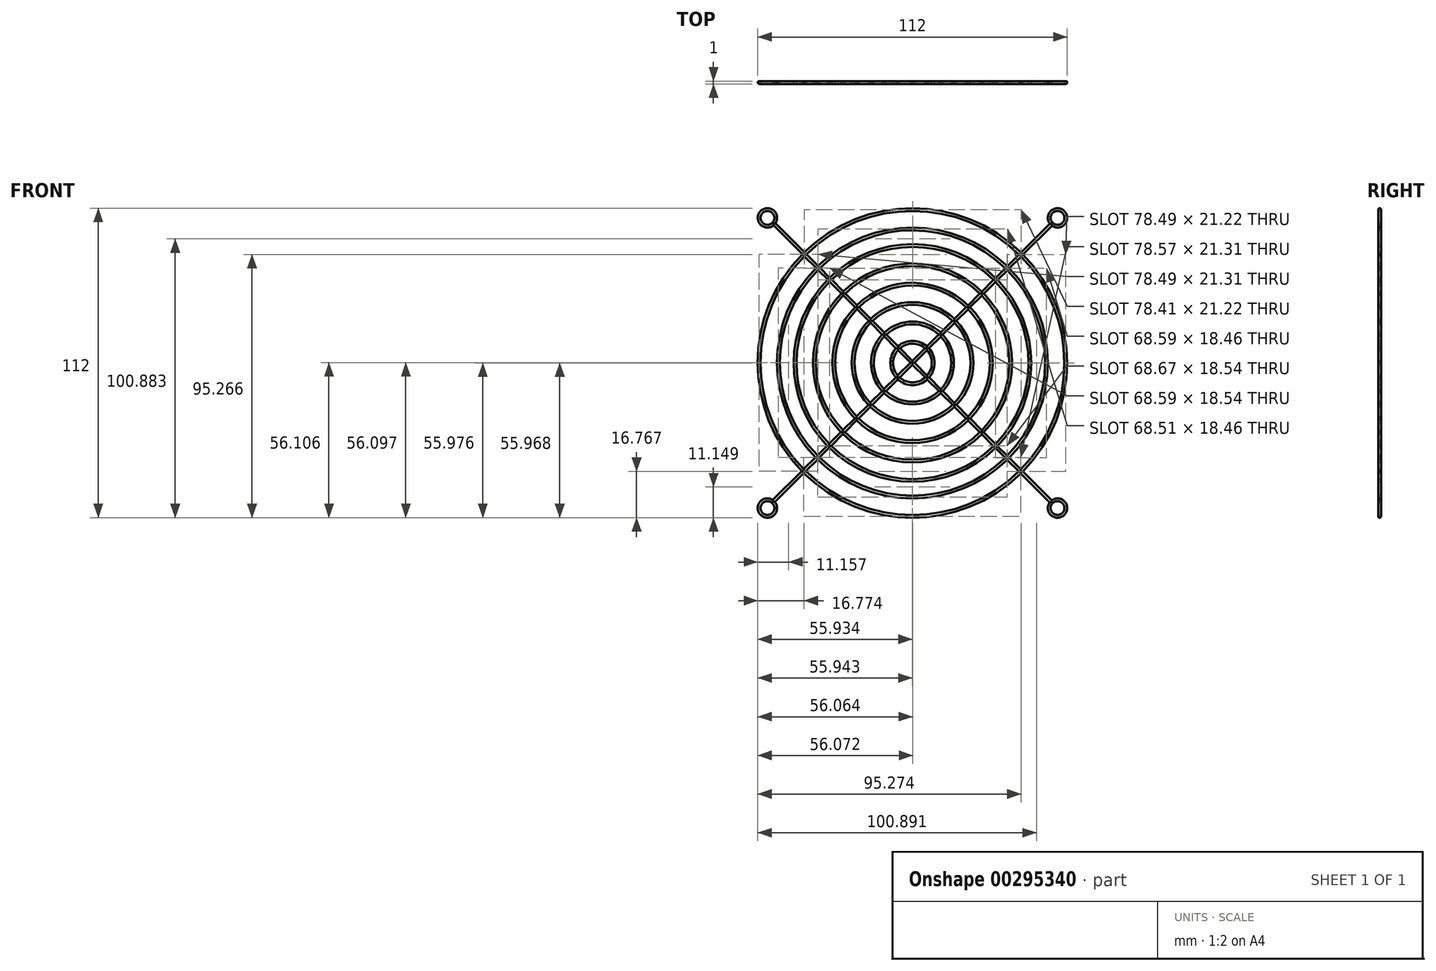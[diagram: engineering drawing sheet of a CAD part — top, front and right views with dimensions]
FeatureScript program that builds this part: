
annotation { "Feature Type Name" : "Feature", "Feature Type Description" : "" }
export const myFeature = defineFeature(function(context is Context, id is Id, definition is map)
    precondition{}
    {
        {
            var Q0;
            Q0=qCreatedBy(makeId("Front.planeOp"),FACE);
            var sketch = newSketch(context, id + "F0", { "sketchPlane" : qUnion([Q0])});
            skCircle(sketch, "E0", {"center": v(-12.88, 1.36) * mm, "radius": 7 * mm});
            skCircle(sketch, "E1", {"center": v(-12.88, 1.36) * mm, "radius": 8 * mm});
            skCircle(sketch, "E2", {"center": v(-12.88, 1.36) * mm, "radius": 14 * mm});
            skCircle(sketch, "E3", {"center": v(-12.88, 1.36) * mm, "radius": 15 * mm});
            skCircle(sketch, "E4", {"center": v(-12.88, 1.36) * mm, "radius": 21 * mm});
            skCircle(sketch, "E5", {"center": v(-12.88, 1.36) * mm, "radius": 22 * mm});
            skCircle(sketch, "E6", {"center": v(-12.88, 1.36) * mm, "radius": 28 * mm});
            skCircle(sketch, "E7", {"center": v(-12.88, 1.36) * mm, "radius": 29 * mm});
            skCircle(sketch, "E8", {"center": v(-12.88, 1.36) * mm, "radius": 35 * mm});
            skCircle(sketch, "E9", {"center": v(-12.88, 1.36) * mm, "radius": 36 * mm});
            skCircle(sketch, "E10", {"center": v(-12.88, 1.36) * mm, "radius": 42 * mm});
            skCircle(sketch, "E11", {"center": v(-12.88, 1.36) * mm, "radius": 43 * mm});
            skCircle(sketch, "E12", {"center": v(-12.88, 1.36) * mm, "radius": 48 * mm});
            skCircle(sketch, "E13", {"center": v(-12.88, 1.36) * mm, "radius": 49 * mm});
            skCircle(sketch, "E14", {"center": v(-12.88, 1.36) * mm, "radius": 55 * mm});
            skCircle(sketch, "E15", {"center": v(-12.88, 1.36) * mm, "radius": 56 * mm});
            skLineSegment(sketch, "E16.bottom", {"start": v(39.62, -51.14) * mm, "end": v(-65.38, -51.14) * mm, "construction": true});
            skLineSegment(sketch, "E16.top", {"start": v(39.62, 53.86) * mm, "end": v(-65.38, 53.86) * mm, "construction": true});
            skLineSegment(sketch, "E16.left", {"start": v(39.62, -51.14) * mm, "end": v(39.62, 53.86) * mm, "construction": true});
            skLineSegment(sketch, "E16.right", {"start": v(-65.38, -51.14) * mm, "end": v(-65.38, 53.86) * mm, "construction": true});
            skCircle(sketch, "E17", {"center": v(-65.38, 53.86) * mm, "radius": 2.5 * mm});
            skCircle(sketch, "E18", {"center": v(39.62, 53.86) * mm, "radius": 2.5 * mm});
            skCircle(sketch, "E19", {"center": v(39.62, -51.14) * mm, "radius": 2.5 * mm});
            skCircle(sketch, "E20", {"center": v(-65.38, -51.14) * mm, "radius": 2.5 * mm});
            skCircle(sketch, "E21", {"center": v(-65.38, 53.86) * mm, "radius": 3.5 * mm});
            skCircle(sketch, "E22", {"center": v(39.62, 53.86) * mm, "radius": 3.5 * mm});
            skCircle(sketch, "E23", {"center": v(39.62, -51.14) * mm, "radius": 3.5 * mm});
            skCircle(sketch, "E24", {"center": v(-65.38, -51.14) * mm, "radius": 3.5 * mm});
            skLineSegment(sketch, "E25", {"start": v(37.2, 51.33) * mm, "end": v(-63.03, -48.54) * mm, "construction": true});
            skLineSegment(sketch, "E26", {"start": v(-12.56, 1.04) * mm, "end": v(-62.69, -48.9) * mm});
            skLineSegment(sketch, "E27", {"start": v(-13.24, 1.78) * mm, "end": v(-63.43, -48.23) * mm});
            skLineSegment(sketch, "E28", {"start": v(-13.24, 1.78) * mm, "end": v(36.86, 51.7) * mm});
            skLineSegment(sketch, "E29", {"start": v(-12.56, 1.04) * mm, "end": v(37.58, 51.01) * mm});
            skLineSegment(sketch, "E30.1.0", {"start": v(-12.46, 1.72) * mm, "end": v(37.47, -48.38) * mm});
            skLineSegment(sketch, "E30.1.1", {"start": v(37.1, -48.72) * mm, "end": v(-62.78, 51.51) * mm, "construction": true});
            skLineSegment(sketch, "E30.1.2", {"start": v(-13.19, 1.04) * mm, "end": v(36.78, -49.1) * mm});
            skLineSegment(sketch, "E30.1.3", {"start": v(-13.19, 1.04) * mm, "end": v(-63.14, 51.17) * mm});
            skLineSegment(sketch, "E30.1.4", {"start": v(-12.46, 1.72) * mm, "end": v(-62.47, 51.91) * mm});
            skLineSegment(sketch, "E30.anchor1", {"start": v(-12.88, 1.36) * mm, "end": v(-12.56, 1.04) * mm, "construction": true});
            skLineSegment(sketch, "E30.anchor2", {"start": v(-12.88, 1.36) * mm, "end": v(-13.19, 1.04) * mm, "construction": true});
            skSolve(sketch);
        }
        {
            var Q0;
            {var subQ0=sQuery(id+"F0.wireOp",EDGE,"E28");var subQ1=sQuery(id+"F0.wireOp",EDGE,"E14");var subQ2=makeQuery(id+"F0.imprint","INTERSECT",VERTEX,{"derivedFrom":[subQ1,subQ0]});Q0=makeQuery(id+"F0.imprint","IMPRINT",FACE,{"disambiguationData":[TD([[makeQuery(id+"F0.imprint","IMPRINT",EDGE,{"disambiguationData":[TD([[subQ2,-1.0]])],"derivedFrom":subQ1}),-1.0]])]});}
            var Q1;
            {var subQ0=sQuery(id+"F0.wireOp",EDGE,"E29");var subQ1=sQuery(id+"F0.wireOp",EDGE,"E14");var subQ2=makeQuery(id+"F0.imprint","INTERSECT",VERTEX,{"derivedFrom":[subQ1,subQ0]});Q1=makeQuery(id+"F0.imprint","IMPRINT",FACE,{"disambiguationData":[TD([[makeQuery(id+"F0.imprint","IMPRINT",EDGE,{"disambiguationData":[TD([[subQ2,1.0]])],"derivedFrom":subQ1}),-1.0]])]});}
            var Q2;
            {var subQ0=sQuery(id+"F0.wireOp",EDGE,"E28");var subQ1=sQuery(id+"F0.wireOp",EDGE,"E15");var subQ2=makeQuery(id+"F0.imprint","INTERSECT",VERTEX,{"derivedFrom":[subQ1,subQ0]});Q2=makeQuery(id+"F0.imprint","IMPRINT",FACE,{"disambiguationData":[TD([[makeQuery(id+"F0.imprint","IMPRINT",EDGE,{"disambiguationData":[TD([[subQ2,1.0]])],"derivedFrom":subQ1}),-1.0]])]});}
            var Q3;
            {var subQ0=sQuery(id+"F0.wireOp",EDGE,"E28");var subQ1=sQuery(id+"F0.wireOp",EDGE,"E13");var subQ2=makeQuery(id+"F0.imprint","INTERSECT",VERTEX,{"derivedFrom":[subQ1,subQ0]});Q3=makeQuery(id+"F0.imprint","IMPRINT",FACE,{"disambiguationData":[TD([[makeQuery(id+"F0.imprint","IMPRINT",EDGE,{"disambiguationData":[TD([[subQ2,1.0]])],"derivedFrom":subQ1}),-1.0]])]});}
            var Q4;
            {var subQ0=sQuery(id+"F0.wireOp",EDGE,"E28");var subQ1=sQuery(id+"F0.wireOp",EDGE,"E14");var subQ2=makeQuery(id+"F0.imprint","INTERSECT",VERTEX,{"derivedFrom":[subQ1,subQ0]});Q4=makeQuery(id+"F0.imprint","IMPRINT",FACE,{"disambiguationData":[TD([[makeQuery(id+"F0.imprint","IMPRINT",EDGE,{"disambiguationData":[TD([[subQ2,1.0]])],"derivedFrom":subQ1}),-1.0]])]});}
            var Q5;
            {var subQ0=sQuery(id+"F0.wireOp",EDGE,"E28");var subQ1=sQuery(id+"F0.wireOp",EDGE,"E12");var subQ2=makeQuery(id+"F0.imprint","INTERSECT",VERTEX,{"derivedFrom":[subQ1,subQ0]});Q5=makeQuery(id+"F0.imprint","IMPRINT",FACE,{"disambiguationData":[TD([[makeQuery(id+"F0.imprint","IMPRINT",EDGE,{"disambiguationData":[TD([[subQ2,-1.0]])],"derivedFrom":subQ1}),-1.0]])]});}
            var Q6;
            {var subQ0=sQuery(id+"F0.wireOp",EDGE,"E29");var subQ1=sQuery(id+"F0.wireOp",EDGE,"E12");var subQ2=makeQuery(id+"F0.imprint","INTERSECT",VERTEX,{"derivedFrom":[subQ1,subQ0]});Q6=makeQuery(id+"F0.imprint","IMPRINT",FACE,{"disambiguationData":[TD([[makeQuery(id+"F0.imprint","IMPRINT",EDGE,{"disambiguationData":[TD([[subQ2,1.0]])],"derivedFrom":subQ1}),-1.0]])]});}
            var Q7;
            {var subQ0=sQuery(id+"F0.wireOp",EDGE,"E28");var subQ1=sQuery(id+"F0.wireOp",EDGE,"E12");var subQ2=makeQuery(id+"F0.imprint","INTERSECT",VERTEX,{"derivedFrom":[subQ1,subQ0]});Q7=makeQuery(id+"F0.imprint","IMPRINT",FACE,{"disambiguationData":[TD([[makeQuery(id+"F0.imprint","IMPRINT",EDGE,{"disambiguationData":[TD([[subQ2,1.0]])],"derivedFrom":subQ1}),-1.0]])]});}
            var Q8;
            {var subQ0=sQuery(id+"F0.wireOp",EDGE,"E28");var subQ1=sQuery(id+"F0.wireOp",EDGE,"E10");var subQ2=makeQuery(id+"F0.imprint","INTERSECT",VERTEX,{"derivedFrom":[subQ1,subQ0]});Q8=makeQuery(id+"F0.imprint","IMPRINT",FACE,{"disambiguationData":[TD([[makeQuery(id+"F0.imprint","IMPRINT",EDGE,{"disambiguationData":[TD([[subQ2,-1.0]])],"derivedFrom":subQ1}),-1.0]])]});}
            var Q9;
            {var subQ0=sQuery(id+"F0.wireOp",EDGE,"E29");var subQ1=sQuery(id+"F0.wireOp",EDGE,"E10");var subQ2=makeQuery(id+"F0.imprint","INTERSECT",VERTEX,{"derivedFrom":[subQ1,subQ0]});Q9=makeQuery(id+"F0.imprint","IMPRINT",FACE,{"disambiguationData":[TD([[makeQuery(id+"F0.imprint","IMPRINT",EDGE,{"disambiguationData":[TD([[subQ2,1.0]])],"derivedFrom":subQ1}),-1.0]])]});}
            var Q10;
            {var subQ0=sQuery(id+"F0.wireOp",EDGE,"E28");var subQ1=sQuery(id+"F0.wireOp",EDGE,"E10");var subQ2=makeQuery(id+"F0.imprint","INTERSECT",VERTEX,{"derivedFrom":[subQ1,subQ0]});Q10=makeQuery(id+"F0.imprint","IMPRINT",FACE,{"disambiguationData":[TD([[makeQuery(id+"F0.imprint","IMPRINT",EDGE,{"disambiguationData":[TD([[subQ2,1.0]])],"derivedFrom":subQ1}),-1.0]])]});}
            var Q11;
            {var subQ0=sQuery(id+"F0.wireOp",EDGE,"E28");var subQ1=sQuery(id+"F0.wireOp",EDGE,"E11");var subQ2=makeQuery(id+"F0.imprint","INTERSECT",VERTEX,{"derivedFrom":[subQ1,subQ0]});Q11=makeQuery(id+"F0.imprint","IMPRINT",FACE,{"disambiguationData":[TD([[makeQuery(id+"F0.imprint","IMPRINT",EDGE,{"disambiguationData":[TD([[subQ2,1.0]])],"derivedFrom":subQ1}),-1.0]])]});}
            var Q12;
            {var subQ0=sQuery(id+"F0.wireOp",EDGE,"E28");var subQ1=sQuery(id+"F0.wireOp",EDGE,"E9");var subQ2=makeQuery(id+"F0.imprint","INTERSECT",VERTEX,{"derivedFrom":[subQ1,subQ0]});Q12=makeQuery(id+"F0.imprint","IMPRINT",FACE,{"disambiguationData":[TD([[makeQuery(id+"F0.imprint","IMPRINT",EDGE,{"disambiguationData":[TD([[subQ2,1.0]])],"derivedFrom":subQ1}),-1.0]])]});}
            var Q13;
            {var subQ0=sQuery(id+"F0.wireOp",EDGE,"E29");var subQ1=sQuery(id+"F0.wireOp",EDGE,"E8");var subQ2=makeQuery(id+"F0.imprint","INTERSECT",VERTEX,{"derivedFrom":[subQ1,subQ0]});Q13=makeQuery(id+"F0.imprint","IMPRINT",FACE,{"disambiguationData":[TD([[makeQuery(id+"F0.imprint","IMPRINT",EDGE,{"disambiguationData":[TD([[subQ2,1.0]])],"derivedFrom":subQ1}),-1.0]])]});}
            var Q14;
            {var subQ0=sQuery(id+"F0.wireOp",EDGE,"E28");var subQ1=sQuery(id+"F0.wireOp",EDGE,"E7");var subQ2=makeQuery(id+"F0.imprint","INTERSECT",VERTEX,{"derivedFrom":[subQ1,subQ0]});Q14=makeQuery(id+"F0.imprint","IMPRINT",FACE,{"disambiguationData":[TD([[makeQuery(id+"F0.imprint","IMPRINT",EDGE,{"disambiguationData":[TD([[subQ2,1.0]])],"derivedFrom":subQ1}),-1.0]])]});}
            var Q15;
            {var subQ0=sQuery(id+"F0.wireOp",EDGE,"E28");var subQ1=sQuery(id+"F0.wireOp",EDGE,"E8");var subQ2=makeQuery(id+"F0.imprint","INTERSECT",VERTEX,{"derivedFrom":[subQ1,subQ0]});Q15=makeQuery(id+"F0.imprint","IMPRINT",FACE,{"disambiguationData":[TD([[makeQuery(id+"F0.imprint","IMPRINT",EDGE,{"disambiguationData":[TD([[subQ2,1.0]])],"derivedFrom":subQ1}),-1.0]])]});}
            var Q16;
            {var subQ0=sQuery(id+"F0.wireOp",EDGE,"E28");var subQ1=sQuery(id+"F0.wireOp",EDGE,"E8");var subQ2=makeQuery(id+"F0.imprint","INTERSECT",VERTEX,{"derivedFrom":[subQ1,subQ0]});Q16=makeQuery(id+"F0.imprint","IMPRINT",FACE,{"disambiguationData":[TD([[makeQuery(id+"F0.imprint","IMPRINT",EDGE,{"disambiguationData":[TD([[subQ2,-1.0]])],"derivedFrom":subQ1}),-1.0]])]});}
            var Q17;
            {var subQ0=sQuery(id+"F0.wireOp",EDGE,"E28");var subQ1=sQuery(id+"F0.wireOp",EDGE,"E6");var subQ2=makeQuery(id+"F0.imprint","INTERSECT",VERTEX,{"derivedFrom":[subQ1,subQ0]});Q17=makeQuery(id+"F0.imprint","IMPRINT",FACE,{"disambiguationData":[TD([[makeQuery(id+"F0.imprint","IMPRINT",EDGE,{"disambiguationData":[TD([[subQ2,-1.0]])],"derivedFrom":subQ1}),-1.0]])]});}
            var Q18;
            {var subQ0=sQuery(id+"F0.wireOp",EDGE,"E29");var subQ1=sQuery(id+"F0.wireOp",EDGE,"E6");var subQ2=makeQuery(id+"F0.imprint","INTERSECT",VERTEX,{"derivedFrom":[subQ1,subQ0]});Q18=makeQuery(id+"F0.imprint","IMPRINT",FACE,{"disambiguationData":[TD([[makeQuery(id+"F0.imprint","IMPRINT",EDGE,{"disambiguationData":[TD([[subQ2,1.0]])],"derivedFrom":subQ1}),-1.0]])]});}
            var Q19;
            {var subQ0=sQuery(id+"F0.wireOp",EDGE,"E28");var subQ1=sQuery(id+"F0.wireOp",EDGE,"E5");var subQ2=makeQuery(id+"F0.imprint","INTERSECT",VERTEX,{"derivedFrom":[subQ1,subQ0]});Q19=makeQuery(id+"F0.imprint","IMPRINT",FACE,{"disambiguationData":[TD([[makeQuery(id+"F0.imprint","IMPRINT",EDGE,{"disambiguationData":[TD([[subQ2,1.0]])],"derivedFrom":subQ1}),-1.0]])]});}
            var Q20;
            {var subQ0=sQuery(id+"F0.wireOp",EDGE,"E28");var subQ1=sQuery(id+"F0.wireOp",EDGE,"E6");var subQ2=makeQuery(id+"F0.imprint","INTERSECT",VERTEX,{"derivedFrom":[subQ1,subQ0]});Q20=makeQuery(id+"F0.imprint","IMPRINT",FACE,{"disambiguationData":[TD([[makeQuery(id+"F0.imprint","IMPRINT",EDGE,{"disambiguationData":[TD([[subQ2,1.0]])],"derivedFrom":subQ1}),-1.0]])]});}
            var Q21;
            {var subQ0=sQuery(id+"F0.wireOp",EDGE,"E28");var subQ1=sQuery(id+"F0.wireOp",EDGE,"E4");var subQ2=makeQuery(id+"F0.imprint","INTERSECT",VERTEX,{"derivedFrom":[subQ1,subQ0]});Q21=makeQuery(id+"F0.imprint","IMPRINT",FACE,{"disambiguationData":[TD([[makeQuery(id+"F0.imprint","IMPRINT",EDGE,{"disambiguationData":[TD([[subQ2,1.0]])],"derivedFrom":subQ1}),-1.0]])]});}
            var Q22;
            {var subQ0=sQuery(id+"F0.wireOp",EDGE,"E29");var subQ1=sQuery(id+"F0.wireOp",EDGE,"E4");var subQ2=makeQuery(id+"F0.imprint","INTERSECT",VERTEX,{"derivedFrom":[subQ1,subQ0]});Q22=makeQuery(id+"F0.imprint","IMPRINT",FACE,{"disambiguationData":[TD([[makeQuery(id+"F0.imprint","IMPRINT",EDGE,{"disambiguationData":[TD([[subQ2,1.0]])],"derivedFrom":subQ1}),-1.0]])]});}
            var Q23;
            {var subQ0=sQuery(id+"F0.wireOp",EDGE,"E28");var subQ1=sQuery(id+"F0.wireOp",EDGE,"E3");var subQ2=makeQuery(id+"F0.imprint","INTERSECT",VERTEX,{"derivedFrom":[subQ1,subQ0]});Q23=makeQuery(id+"F0.imprint","IMPRINT",FACE,{"disambiguationData":[TD([[makeQuery(id+"F0.imprint","IMPRINT",EDGE,{"disambiguationData":[TD([[subQ2,1.0]])],"derivedFrom":subQ1}),-1.0]])]});}
            var Q24;
            {var subQ0=sQuery(id+"F0.wireOp",EDGE,"E28");var subQ1=sQuery(id+"F0.wireOp",EDGE,"E4");var subQ2=makeQuery(id+"F0.imprint","INTERSECT",VERTEX,{"derivedFrom":[subQ1,subQ0]});Q24=makeQuery(id+"F0.imprint","IMPRINT",FACE,{"disambiguationData":[TD([[makeQuery(id+"F0.imprint","IMPRINT",EDGE,{"disambiguationData":[TD([[subQ2,-1.0]])],"derivedFrom":subQ1}),-1.0]])]});}
            var Q25;
            {var subQ0=sQuery(id+"F0.wireOp",EDGE,"E28");var subQ1=sQuery(id+"F0.wireOp",EDGE,"E2");var subQ2=makeQuery(id+"F0.imprint","INTERSECT",VERTEX,{"derivedFrom":[subQ1,subQ0]});Q25=makeQuery(id+"F0.imprint","IMPRINT",FACE,{"disambiguationData":[TD([[makeQuery(id+"F0.imprint","IMPRINT",EDGE,{"disambiguationData":[TD([[subQ2,1.0]])],"derivedFrom":subQ1}),-1.0]])]});}
            var Q26;
            {var subQ0=sQuery(id+"F0.wireOp",EDGE,"E29");var subQ1=sQuery(id+"F0.wireOp",EDGE,"E2");var subQ2=makeQuery(id+"F0.imprint","INTERSECT",VERTEX,{"derivedFrom":[subQ1,subQ0]});Q26=makeQuery(id+"F0.imprint","IMPRINT",FACE,{"disambiguationData":[TD([[makeQuery(id+"F0.imprint","IMPRINT",EDGE,{"disambiguationData":[TD([[subQ2,1.0]])],"derivedFrom":subQ1}),-1.0]])]});}
            var Q27;
            {var subQ0=sQuery(id+"F0.wireOp",EDGE,"E28");var subQ1=sQuery(id+"F0.wireOp",EDGE,"E2");var subQ2=makeQuery(id+"F0.imprint","INTERSECT",VERTEX,{"derivedFrom":[subQ1,subQ0]});Q27=makeQuery(id+"F0.imprint","IMPRINT",FACE,{"disambiguationData":[TD([[makeQuery(id+"F0.imprint","IMPRINT",EDGE,{"disambiguationData":[TD([[subQ2,-1.0]])],"derivedFrom":subQ1}),-1.0]])]});}
            var Q28;
            {var subQ0=sQuery(id+"F0.wireOp",EDGE,"E28");var subQ1=sQuery(id+"F0.wireOp",EDGE,"E1");var subQ2=makeQuery(id+"F0.imprint","INTERSECT",VERTEX,{"derivedFrom":[subQ1,subQ0]});Q28=makeQuery(id+"F0.imprint","IMPRINT",FACE,{"disambiguationData":[TD([[makeQuery(id+"F0.imprint","IMPRINT",EDGE,{"disambiguationData":[TD([[subQ2,1.0]])],"derivedFrom":subQ1}),-1.0]])]});}
            var Q29;
            {var subQ0=sQuery(id+"F0.wireOp",EDGE,"E28");var subQ1=sQuery(id+"F0.wireOp",EDGE,"E0");var subQ2=makeQuery(id+"F0.imprint","INTERSECT",VERTEX,{"derivedFrom":[subQ1,subQ0]});Q29=makeQuery(id+"F0.imprint","IMPRINT",FACE,{"disambiguationData":[TD([[makeQuery(id+"F0.imprint","IMPRINT",EDGE,{"disambiguationData":[TD([[subQ2,-1.0]])],"derivedFrom":subQ1}),-1.0]])]});}
            var Q30;
            {var subQ0=sQuery(id+"F0.wireOp",EDGE,"E29");var subQ1=sQuery(id+"F0.wireOp",EDGE,"E0");var subQ2=makeQuery(id+"F0.imprint","INTERSECT",VERTEX,{"derivedFrom":[subQ1,subQ0]});Q30=makeQuery(id+"F0.imprint","IMPRINT",FACE,{"disambiguationData":[TD([[makeQuery(id+"F0.imprint","IMPRINT",EDGE,{"disambiguationData":[TD([[subQ2,1.0]])],"derivedFrom":subQ1}),-1.0]])]});}
            var Q31;
            {var subQ0=sQuery(id+"F0.wireOp",EDGE,"E28");var subQ1=sQuery(id+"F0.wireOp",EDGE,"E0");var subQ2=makeQuery(id+"F0.imprint","INTERSECT",VERTEX,{"derivedFrom":[subQ1,subQ0]});Q31=makeQuery(id+"F0.imprint","IMPRINT",FACE,{"disambiguationData":[TD([[makeQuery(id+"F0.imprint","IMPRINT",EDGE,{"disambiguationData":[TD([[subQ2,1.0]])],"derivedFrom":subQ1}),-1.0]])]});}
            var Q32;
            {var subQ5=sQuery(id+"F0.wireOp",EDGE,"E28");var subQ6=sQuery(id+"F0.wireOp",EDGE,"E0");var subQ7=makeQuery(id+"F0.imprint","INTERSECT",VERTEX,{"derivedFrom":[subQ6,subQ5]});Q32=makeQuery(id+"F0.imprint","IMPRINT",FACE,{"disambiguationData":[TD([[makeQuery(id+"F0.imprint","IMPRINT",EDGE,{"disambiguationData":[TD([[subQ7,1.0]])],"derivedFrom":subQ6}),1.0]])]});}
            var Q33;
            {var subQ0=sQuery(id+"F0.wireOp",EDGE,"E29");var subQ1=sQuery(id+"F0.wireOp",EDGE,"E26");var subQ2=makeQuery(id+"F0.imprint","INTERSECT",VERTEX,{"derivedFrom":[subQ1,subQ0]});Q33=makeQuery(id+"F0.imprint","IMPRINT",FACE,{"disambiguationData":[TD([[makeQuery(id+"F0.imprint","IMPRINT",EDGE,{"disambiguationData":[TD([[subQ2,-1.0]])],"derivedFrom":subQ1}),-1.0]])]});}
            var Q34;
            {var subQ1=sQuery(id+"F0.wireOp",EDGE,"E0");var subQ7=sQuery(id+"F0.wireOp",EDGE,"E30.1.4");var subQ9=makeQuery(id+"F0.imprint","INTERSECT",VERTEX,{"derivedFrom":[subQ1,subQ7]});Q34=makeQuery(id+"F0.imprint","IMPRINT",FACE,{"disambiguationData":[TD([[makeQuery(id+"F0.imprint","IMPRINT",EDGE,{"disambiguationData":[TD([[subQ9,-1.0]])],"derivedFrom":subQ1}),1.0]])]});}
            var Q35;
            {var subQ1=sQuery(id+"F0.wireOp",EDGE,"E0");var subQ7=sQuery(id+"F0.wireOp",EDGE,"E30.1.2");var subQ9=makeQuery(id+"F0.imprint","INTERSECT",VERTEX,{"derivedFrom":[subQ1,subQ7]});Q35=makeQuery(id+"F0.imprint","IMPRINT",FACE,{"disambiguationData":[TD([[makeQuery(id+"F0.imprint","IMPRINT",EDGE,{"disambiguationData":[TD([[subQ9,-1.0]])],"derivedFrom":subQ1}),1.0]])]});}
            var Q36;
            {var subQ5=sQuery(id+"F0.wireOp",EDGE,"E0");var subQ7=sQuery(id+"F0.wireOp",EDGE,"E27");var subQ8=makeQuery(id+"F0.imprint","INTERSECT",VERTEX,{"derivedFrom":[subQ5,subQ7]});Q36=makeQuery(id+"F0.imprint","IMPRINT",FACE,{"disambiguationData":[TD([[makeQuery(id+"F0.imprint","IMPRINT",EDGE,{"disambiguationData":[TD([[subQ8,-1.0]])],"derivedFrom":subQ5}),1.0]])]});}
            var Q37;
            {var subQ0=sQuery(id+"F0.wireOp",EDGE,"E30.1.4");var subQ1=sQuery(id+"F0.wireOp",EDGE,"E0");var subQ2=makeQuery(id+"F0.imprint","INTERSECT",VERTEX,{"derivedFrom":[subQ1,subQ0]});Q37=makeQuery(id+"F0.imprint","IMPRINT",FACE,{"disambiguationData":[TD([[makeQuery(id+"F0.imprint","IMPRINT",EDGE,{"disambiguationData":[TD([[subQ2,-1.0]])],"derivedFrom":subQ1}),-1.0]])]});}
            var Q38;
            {var subQ0=sQuery(id+"F0.wireOp",EDGE,"E30.1.3");var subQ1=sQuery(id+"F0.wireOp",EDGE,"E0");var subQ2=makeQuery(id+"F0.imprint","INTERSECT",VERTEX,{"derivedFrom":[subQ1,subQ0]});Q38=makeQuery(id+"F0.imprint","IMPRINT",FACE,{"disambiguationData":[TD([[makeQuery(id+"F0.imprint","IMPRINT",EDGE,{"disambiguationData":[TD([[subQ2,-1.0]])],"derivedFrom":subQ1}),-1.0]])]});}
            var Q39;
            {var subQ0=sQuery(id+"F0.wireOp",EDGE,"E30.1.4");var subQ1=sQuery(id+"F0.wireOp",EDGE,"E1");var subQ2=makeQuery(id+"F0.imprint","INTERSECT",VERTEX,{"derivedFrom":[subQ1,subQ0]});Q39=makeQuery(id+"F0.imprint","IMPRINT",FACE,{"disambiguationData":[TD([[makeQuery(id+"F0.imprint","IMPRINT",EDGE,{"disambiguationData":[TD([[subQ2,-1.0]])],"derivedFrom":subQ1}),-1.0]])]});}
            var Q40;
            {var subQ0=sQuery(id+"F0.wireOp",EDGE,"E30.1.3");var subQ1=sQuery(id+"F0.wireOp",EDGE,"E2");var subQ2=makeQuery(id+"F0.imprint","INTERSECT",VERTEX,{"derivedFrom":[subQ1,subQ0]});Q40=makeQuery(id+"F0.imprint","IMPRINT",FACE,{"disambiguationData":[TD([[makeQuery(id+"F0.imprint","IMPRINT",EDGE,{"disambiguationData":[TD([[subQ2,-1.0]])],"derivedFrom":subQ1}),-1.0]])]});}
            var Q41;
            {var subQ0=sQuery(id+"F0.wireOp",EDGE,"E30.1.4");var subQ1=sQuery(id+"F0.wireOp",EDGE,"E2");var subQ2=makeQuery(id+"F0.imprint","INTERSECT",VERTEX,{"derivedFrom":[subQ1,subQ0]});Q41=makeQuery(id+"F0.imprint","IMPRINT",FACE,{"disambiguationData":[TD([[makeQuery(id+"F0.imprint","IMPRINT",EDGE,{"disambiguationData":[TD([[subQ2,-1.0]])],"derivedFrom":subQ1}),-1.0]])]});}
            var Q42;
            {var subQ0=sQuery(id+"F0.wireOp",EDGE,"E30.1.4");var subQ1=sQuery(id+"F0.wireOp",EDGE,"E3");var subQ2=makeQuery(id+"F0.imprint","INTERSECT",VERTEX,{"derivedFrom":[subQ1,subQ0]});Q42=makeQuery(id+"F0.imprint","IMPRINT",FACE,{"disambiguationData":[TD([[makeQuery(id+"F0.imprint","IMPRINT",EDGE,{"disambiguationData":[TD([[subQ2,-1.0]])],"derivedFrom":subQ1}),-1.0]])]});}
            var Q43;
            {var subQ0=sQuery(id+"F0.wireOp",EDGE,"E30.1.4");var subQ1=sQuery(id+"F0.wireOp",EDGE,"E4");var subQ2=makeQuery(id+"F0.imprint","INTERSECT",VERTEX,{"derivedFrom":[subQ1,subQ0]});Q43=makeQuery(id+"F0.imprint","IMPRINT",FACE,{"disambiguationData":[TD([[makeQuery(id+"F0.imprint","IMPRINT",EDGE,{"disambiguationData":[TD([[subQ2,-1.0]])],"derivedFrom":subQ1}),-1.0]])]});}
            var Q44;
            {var subQ0=sQuery(id+"F0.wireOp",EDGE,"E30.1.3");var subQ1=sQuery(id+"F0.wireOp",EDGE,"E4");var subQ2=makeQuery(id+"F0.imprint","INTERSECT",VERTEX,{"derivedFrom":[subQ1,subQ0]});Q44=makeQuery(id+"F0.imprint","IMPRINT",FACE,{"disambiguationData":[TD([[makeQuery(id+"F0.imprint","IMPRINT",EDGE,{"disambiguationData":[TD([[subQ2,-1.0]])],"derivedFrom":subQ1}),-1.0]])]});}
            var Q45;
            {var subQ0=sQuery(id+"F0.wireOp",EDGE,"E30.1.4");var subQ1=sQuery(id+"F0.wireOp",EDGE,"E5");var subQ2=makeQuery(id+"F0.imprint","INTERSECT",VERTEX,{"derivedFrom":[subQ1,subQ0]});Q45=makeQuery(id+"F0.imprint","IMPRINT",FACE,{"disambiguationData":[TD([[makeQuery(id+"F0.imprint","IMPRINT",EDGE,{"disambiguationData":[TD([[subQ2,-1.0]])],"derivedFrom":subQ1}),-1.0]])]});}
            var Q46;
            {var subQ0=sQuery(id+"F0.wireOp",EDGE,"E30.1.3");var subQ1=sQuery(id+"F0.wireOp",EDGE,"E6");var subQ2=makeQuery(id+"F0.imprint","INTERSECT",VERTEX,{"derivedFrom":[subQ1,subQ0]});Q46=makeQuery(id+"F0.imprint","IMPRINT",FACE,{"disambiguationData":[TD([[makeQuery(id+"F0.imprint","IMPRINT",EDGE,{"disambiguationData":[TD([[subQ2,-1.0]])],"derivedFrom":subQ1}),-1.0]])]});}
            var Q47;
            {var subQ0=sQuery(id+"F0.wireOp",EDGE,"E30.1.4");var subQ1=sQuery(id+"F0.wireOp",EDGE,"E6");var subQ2=makeQuery(id+"F0.imprint","INTERSECT",VERTEX,{"derivedFrom":[subQ1,subQ0]});Q47=makeQuery(id+"F0.imprint","IMPRINT",FACE,{"disambiguationData":[TD([[makeQuery(id+"F0.imprint","IMPRINT",EDGE,{"disambiguationData":[TD([[subQ2,-1.0]])],"derivedFrom":subQ1}),-1.0]])]});}
            var Q48;
            {var subQ0=sQuery(id+"F0.wireOp",EDGE,"E30.1.4");var subQ1=sQuery(id+"F0.wireOp",EDGE,"E7");var subQ2=makeQuery(id+"F0.imprint","INTERSECT",VERTEX,{"derivedFrom":[subQ1,subQ0]});Q48=makeQuery(id+"F0.imprint","IMPRINT",FACE,{"disambiguationData":[TD([[makeQuery(id+"F0.imprint","IMPRINT",EDGE,{"disambiguationData":[TD([[subQ2,-1.0]])],"derivedFrom":subQ1}),-1.0]])]});}
            var Q49;
            {var subQ0=sQuery(id+"F0.wireOp",EDGE,"E30.1.4");var subQ1=sQuery(id+"F0.wireOp",EDGE,"E8");var subQ2=makeQuery(id+"F0.imprint","INTERSECT",VERTEX,{"derivedFrom":[subQ1,subQ0]});Q49=makeQuery(id+"F0.imprint","IMPRINT",FACE,{"disambiguationData":[TD([[makeQuery(id+"F0.imprint","IMPRINT",EDGE,{"disambiguationData":[TD([[subQ2,-1.0]])],"derivedFrom":subQ1}),-1.0]])]});}
            var Q50;
            {var subQ0=sQuery(id+"F0.wireOp",EDGE,"E30.1.3");var subQ1=sQuery(id+"F0.wireOp",EDGE,"E8");var subQ2=makeQuery(id+"F0.imprint","INTERSECT",VERTEX,{"derivedFrom":[subQ1,subQ0]});Q50=makeQuery(id+"F0.imprint","IMPRINT",FACE,{"disambiguationData":[TD([[makeQuery(id+"F0.imprint","IMPRINT",EDGE,{"disambiguationData":[TD([[subQ2,-1.0]])],"derivedFrom":subQ1}),-1.0]])]});}
            var Q51;
            {var subQ0=sQuery(id+"F0.wireOp",EDGE,"E30.1.4");var subQ1=sQuery(id+"F0.wireOp",EDGE,"E9");var subQ2=makeQuery(id+"F0.imprint","INTERSECT",VERTEX,{"derivedFrom":[subQ1,subQ0]});Q51=makeQuery(id+"F0.imprint","IMPRINT",FACE,{"disambiguationData":[TD([[makeQuery(id+"F0.imprint","IMPRINT",EDGE,{"disambiguationData":[TD([[subQ2,-1.0]])],"derivedFrom":subQ1}),-1.0]])]});}
            var Q52;
            {var subQ0=sQuery(id+"F0.wireOp",EDGE,"E30.1.4");var subQ1=sQuery(id+"F0.wireOp",EDGE,"E10");var subQ2=makeQuery(id+"F0.imprint","INTERSECT",VERTEX,{"derivedFrom":[subQ1,subQ0]});Q52=makeQuery(id+"F0.imprint","IMPRINT",FACE,{"disambiguationData":[TD([[makeQuery(id+"F0.imprint","IMPRINT",EDGE,{"disambiguationData":[TD([[subQ2,-1.0]])],"derivedFrom":subQ1}),-1.0]])]});}
            var Q53;
            {var subQ0=sQuery(id+"F0.wireOp",EDGE,"E30.1.3");var subQ1=sQuery(id+"F0.wireOp",EDGE,"E10");var subQ2=makeQuery(id+"F0.imprint","INTERSECT",VERTEX,{"derivedFrom":[subQ1,subQ0]});Q53=makeQuery(id+"F0.imprint","IMPRINT",FACE,{"disambiguationData":[TD([[makeQuery(id+"F0.imprint","IMPRINT",EDGE,{"disambiguationData":[TD([[subQ2,-1.0]])],"derivedFrom":subQ1}),-1.0]])]});}
            var Q54;
            {var subQ0=sQuery(id+"F0.wireOp",EDGE,"E30.1.4");var subQ1=sQuery(id+"F0.wireOp",EDGE,"E11");var subQ2=makeQuery(id+"F0.imprint","INTERSECT",VERTEX,{"derivedFrom":[subQ1,subQ0]});Q54=makeQuery(id+"F0.imprint","IMPRINT",FACE,{"disambiguationData":[TD([[makeQuery(id+"F0.imprint","IMPRINT",EDGE,{"disambiguationData":[TD([[subQ2,-1.0]])],"derivedFrom":subQ1}),-1.0]])]});}
            var Q55;
            {var subQ0=sQuery(id+"F0.wireOp",EDGE,"E30.1.4");var subQ1=sQuery(id+"F0.wireOp",EDGE,"E12");var subQ2=makeQuery(id+"F0.imprint","INTERSECT",VERTEX,{"derivedFrom":[subQ1,subQ0]});Q55=makeQuery(id+"F0.imprint","IMPRINT",FACE,{"disambiguationData":[TD([[makeQuery(id+"F0.imprint","IMPRINT",EDGE,{"disambiguationData":[TD([[subQ2,-1.0]])],"derivedFrom":subQ1}),-1.0]])]});}
            var Q56;
            {var subQ0=sQuery(id+"F0.wireOp",EDGE,"E30.1.3");var subQ1=sQuery(id+"F0.wireOp",EDGE,"E12");var subQ2=makeQuery(id+"F0.imprint","INTERSECT",VERTEX,{"derivedFrom":[subQ1,subQ0]});Q56=makeQuery(id+"F0.imprint","IMPRINT",FACE,{"disambiguationData":[TD([[makeQuery(id+"F0.imprint","IMPRINT",EDGE,{"disambiguationData":[TD([[subQ2,-1.0]])],"derivedFrom":subQ1}),-1.0]])]});}
            var Q57;
            {var subQ0=sQuery(id+"F0.wireOp",EDGE,"E30.1.4");var subQ1=sQuery(id+"F0.wireOp",EDGE,"E13");var subQ2=makeQuery(id+"F0.imprint","INTERSECT",VERTEX,{"derivedFrom":[subQ1,subQ0]});Q57=makeQuery(id+"F0.imprint","IMPRINT",FACE,{"disambiguationData":[TD([[makeQuery(id+"F0.imprint","IMPRINT",EDGE,{"disambiguationData":[TD([[subQ2,-1.0]])],"derivedFrom":subQ1}),-1.0]])]});}
            var Q58;
            {var subQ0=sQuery(id+"F0.wireOp",EDGE,"E30.1.4");var subQ1=sQuery(id+"F0.wireOp",EDGE,"E14");var subQ2=makeQuery(id+"F0.imprint","INTERSECT",VERTEX,{"derivedFrom":[subQ1,subQ0]});Q58=makeQuery(id+"F0.imprint","IMPRINT",FACE,{"disambiguationData":[TD([[makeQuery(id+"F0.imprint","IMPRINT",EDGE,{"disambiguationData":[TD([[subQ2,-1.0]])],"derivedFrom":subQ1}),-1.0]])]});}
            var Q59;
            {var subQ0=sQuery(id+"F0.wireOp",EDGE,"E30.1.3");var subQ1=sQuery(id+"F0.wireOp",EDGE,"E14");var subQ2=makeQuery(id+"F0.imprint","INTERSECT",VERTEX,{"derivedFrom":[subQ1,subQ0]});Q59=makeQuery(id+"F0.imprint","IMPRINT",FACE,{"disambiguationData":[TD([[makeQuery(id+"F0.imprint","IMPRINT",EDGE,{"disambiguationData":[TD([[subQ2,-1.0]])],"derivedFrom":subQ1}),-1.0]])]});}
            var Q60;
            {var subQ0=sQuery(id+"F0.wireOp",EDGE,"E30.1.4");var subQ1=sQuery(id+"F0.wireOp",EDGE,"E15");var subQ2=makeQuery(id+"F0.imprint","INTERSECT",VERTEX,{"derivedFrom":[subQ1,subQ0]});Q60=makeQuery(id+"F0.imprint","IMPRINT",FACE,{"disambiguationData":[TD([[makeQuery(id+"F0.imprint","IMPRINT",EDGE,{"disambiguationData":[TD([[subQ2,-1.0]])],"derivedFrom":subQ1}),-1.0]])]});}
            var Q61;
            Q61=makeQuery(id+"F0.imprint","IMPRINT",FACE,{"disambiguationData":[TD([[makeQuery(id+"F0.imprint","IMPRINT",EDGE,{"derivedFrom":sQuery(id+"F0.wireOp",EDGE,"E17")}),-1.0]])]});
            var Q62;
            Q62=makeQuery(id+"F0.imprint","IMPRINT",FACE,{"disambiguationData":[TD([[makeQuery(id+"F0.imprint","IMPRINT",EDGE,{"derivedFrom":sQuery(id+"F0.wireOp",EDGE,"E18")}),-1.0]])]});
            var Q63;
            {var subQ0=sQuery(id+"F0.wireOp",EDGE,"E26");var subQ1=sQuery(id+"F0.wireOp",EDGE,"E0");var subQ2=makeQuery(id+"F0.imprint","INTERSECT",VERTEX,{"derivedFrom":[subQ1,subQ0]});Q63=makeQuery(id+"F0.imprint","IMPRINT",FACE,{"disambiguationData":[TD([[makeQuery(id+"F0.imprint","IMPRINT",EDGE,{"disambiguationData":[TD([[subQ2,-1.0]])],"derivedFrom":subQ1}),-1.0]])]});}
            var Q64;
            {var subQ0=sQuery(id+"F0.wireOp",EDGE,"E30.1.2");var subQ1=sQuery(id+"F0.wireOp",EDGE,"E0");var subQ2=makeQuery(id+"F0.imprint","INTERSECT",VERTEX,{"derivedFrom":[subQ1,subQ0]});Q64=makeQuery(id+"F0.imprint","IMPRINT",FACE,{"disambiguationData":[TD([[makeQuery(id+"F0.imprint","IMPRINT",EDGE,{"disambiguationData":[TD([[subQ2,-1.0]])],"derivedFrom":subQ1}),-1.0]])]});}
            var Q65;
            {var subQ0=sQuery(id+"F0.wireOp",EDGE,"E30.1.2");var subQ1=sQuery(id+"F0.wireOp",EDGE,"E1");var subQ2=makeQuery(id+"F0.imprint","INTERSECT",VERTEX,{"derivedFrom":[subQ1,subQ0]});Q65=makeQuery(id+"F0.imprint","IMPRINT",FACE,{"disambiguationData":[TD([[makeQuery(id+"F0.imprint","IMPRINT",EDGE,{"disambiguationData":[TD([[subQ2,-1.0]])],"derivedFrom":subQ1}),-1.0]])]});}
            var Q66;
            {var subQ0=sQuery(id+"F0.wireOp",EDGE,"E26");var subQ1=sQuery(id+"F0.wireOp",EDGE,"E2");var subQ2=makeQuery(id+"F0.imprint","INTERSECT",VERTEX,{"derivedFrom":[subQ1,subQ0]});Q66=makeQuery(id+"F0.imprint","IMPRINT",FACE,{"disambiguationData":[TD([[makeQuery(id+"F0.imprint","IMPRINT",EDGE,{"disambiguationData":[TD([[subQ2,-1.0]])],"derivedFrom":subQ1}),-1.0]])]});}
            var Q67;
            {var subQ0=sQuery(id+"F0.wireOp",EDGE,"E30.1.2");var subQ1=sQuery(id+"F0.wireOp",EDGE,"E2");var subQ2=makeQuery(id+"F0.imprint","INTERSECT",VERTEX,{"derivedFrom":[subQ1,subQ0]});Q67=makeQuery(id+"F0.imprint","IMPRINT",FACE,{"disambiguationData":[TD([[makeQuery(id+"F0.imprint","IMPRINT",EDGE,{"disambiguationData":[TD([[subQ2,-1.0]])],"derivedFrom":subQ1}),-1.0]])]});}
            var Q68;
            {var subQ0=sQuery(id+"F0.wireOp",EDGE,"E30.1.2");var subQ1=sQuery(id+"F0.wireOp",EDGE,"E3");var subQ2=makeQuery(id+"F0.imprint","INTERSECT",VERTEX,{"derivedFrom":[subQ1,subQ0]});Q68=makeQuery(id+"F0.imprint","IMPRINT",FACE,{"disambiguationData":[TD([[makeQuery(id+"F0.imprint","IMPRINT",EDGE,{"disambiguationData":[TD([[subQ2,-1.0]])],"derivedFrom":subQ1}),-1.0]])]});}
            var Q69;
            {var subQ0=sQuery(id+"F0.wireOp",EDGE,"E30.1.2");var subQ1=sQuery(id+"F0.wireOp",EDGE,"E4");var subQ2=makeQuery(id+"F0.imprint","INTERSECT",VERTEX,{"derivedFrom":[subQ1,subQ0]});Q69=makeQuery(id+"F0.imprint","IMPRINT",FACE,{"disambiguationData":[TD([[makeQuery(id+"F0.imprint","IMPRINT",EDGE,{"disambiguationData":[TD([[subQ2,-1.0]])],"derivedFrom":subQ1}),-1.0]])]});}
            var Q70;
            {var subQ0=sQuery(id+"F0.wireOp",EDGE,"E30.1.2");var subQ1=sQuery(id+"F0.wireOp",EDGE,"E5");var subQ2=makeQuery(id+"F0.imprint","INTERSECT",VERTEX,{"derivedFrom":[subQ1,subQ0]});Q70=makeQuery(id+"F0.imprint","IMPRINT",FACE,{"disambiguationData":[TD([[makeQuery(id+"F0.imprint","IMPRINT",EDGE,{"disambiguationData":[TD([[subQ2,-1.0]])],"derivedFrom":subQ1}),-1.0]])]});}
            var Q71;
            {var subQ0=sQuery(id+"F0.wireOp",EDGE,"E26");var subQ1=sQuery(id+"F0.wireOp",EDGE,"E4");var subQ2=makeQuery(id+"F0.imprint","INTERSECT",VERTEX,{"derivedFrom":[subQ1,subQ0]});Q71=makeQuery(id+"F0.imprint","IMPRINT",FACE,{"disambiguationData":[TD([[makeQuery(id+"F0.imprint","IMPRINT",EDGE,{"disambiguationData":[TD([[subQ2,-1.0]])],"derivedFrom":subQ1}),-1.0]])]});}
            var Q72;
            {var subQ0=sQuery(id+"F0.wireOp",EDGE,"E30.1.2");var subQ1=sQuery(id+"F0.wireOp",EDGE,"E6");var subQ2=makeQuery(id+"F0.imprint","INTERSECT",VERTEX,{"derivedFrom":[subQ1,subQ0]});Q72=makeQuery(id+"F0.imprint","IMPRINT",FACE,{"disambiguationData":[TD([[makeQuery(id+"F0.imprint","IMPRINT",EDGE,{"disambiguationData":[TD([[subQ2,-1.0]])],"derivedFrom":subQ1}),-1.0]])]});}
            var Q73;
            {var subQ0=sQuery(id+"F0.wireOp",EDGE,"E30.1.2");var subQ1=sQuery(id+"F0.wireOp",EDGE,"E7");var subQ2=makeQuery(id+"F0.imprint","INTERSECT",VERTEX,{"derivedFrom":[subQ1,subQ0]});Q73=makeQuery(id+"F0.imprint","IMPRINT",FACE,{"disambiguationData":[TD([[makeQuery(id+"F0.imprint","IMPRINT",EDGE,{"disambiguationData":[TD([[subQ2,-1.0]])],"derivedFrom":subQ1}),-1.0]])]});}
            var Q74;
            {var subQ0=sQuery(id+"F0.wireOp",EDGE,"E26");var subQ1=sQuery(id+"F0.wireOp",EDGE,"E6");var subQ2=makeQuery(id+"F0.imprint","INTERSECT",VERTEX,{"derivedFrom":[subQ1,subQ0]});Q74=makeQuery(id+"F0.imprint","IMPRINT",FACE,{"disambiguationData":[TD([[makeQuery(id+"F0.imprint","IMPRINT",EDGE,{"disambiguationData":[TD([[subQ2,-1.0]])],"derivedFrom":subQ1}),-1.0]])]});}
            var Q75;
            {var subQ0=sQuery(id+"F0.wireOp",EDGE,"E30.1.2");var subQ1=sQuery(id+"F0.wireOp",EDGE,"E8");var subQ2=makeQuery(id+"F0.imprint","INTERSECT",VERTEX,{"derivedFrom":[subQ1,subQ0]});Q75=makeQuery(id+"F0.imprint","IMPRINT",FACE,{"disambiguationData":[TD([[makeQuery(id+"F0.imprint","IMPRINT",EDGE,{"disambiguationData":[TD([[subQ2,-1.0]])],"derivedFrom":subQ1}),-1.0]])]});}
            var Q76;
            {var subQ0=sQuery(id+"F0.wireOp",EDGE,"E26");var subQ1=sQuery(id+"F0.wireOp",EDGE,"E8");var subQ2=makeQuery(id+"F0.imprint","INTERSECT",VERTEX,{"derivedFrom":[subQ1,subQ0]});Q76=makeQuery(id+"F0.imprint","IMPRINT",FACE,{"disambiguationData":[TD([[makeQuery(id+"F0.imprint","IMPRINT",EDGE,{"disambiguationData":[TD([[subQ2,-1.0]])],"derivedFrom":subQ1}),-1.0]])]});}
            var Q77;
            {var subQ0=sQuery(id+"F0.wireOp",EDGE,"E30.1.2");var subQ1=sQuery(id+"F0.wireOp",EDGE,"E9");var subQ2=makeQuery(id+"F0.imprint","INTERSECT",VERTEX,{"derivedFrom":[subQ1,subQ0]});Q77=makeQuery(id+"F0.imprint","IMPRINT",FACE,{"disambiguationData":[TD([[makeQuery(id+"F0.imprint","IMPRINT",EDGE,{"disambiguationData":[TD([[subQ2,-1.0]])],"derivedFrom":subQ1}),-1.0]])]});}
            var Q78;
            {var subQ0=sQuery(id+"F0.wireOp",EDGE,"E30.1.2");var subQ1=sQuery(id+"F0.wireOp",EDGE,"E10");var subQ2=makeQuery(id+"F0.imprint","INTERSECT",VERTEX,{"derivedFrom":[subQ1,subQ0]});Q78=makeQuery(id+"F0.imprint","IMPRINT",FACE,{"disambiguationData":[TD([[makeQuery(id+"F0.imprint","IMPRINT",EDGE,{"disambiguationData":[TD([[subQ2,-1.0]])],"derivedFrom":subQ1}),-1.0]])]});}
            var Q79;
            {var subQ0=sQuery(id+"F0.wireOp",EDGE,"E26");var subQ1=sQuery(id+"F0.wireOp",EDGE,"E10");var subQ2=makeQuery(id+"F0.imprint","INTERSECT",VERTEX,{"derivedFrom":[subQ1,subQ0]});Q79=makeQuery(id+"F0.imprint","IMPRINT",FACE,{"disambiguationData":[TD([[makeQuery(id+"F0.imprint","IMPRINT",EDGE,{"disambiguationData":[TD([[subQ2,-1.0]])],"derivedFrom":subQ1}),-1.0]])]});}
            var Q80;
            {var subQ0=sQuery(id+"F0.wireOp",EDGE,"E30.1.2");var subQ1=sQuery(id+"F0.wireOp",EDGE,"E11");var subQ2=makeQuery(id+"F0.imprint","INTERSECT",VERTEX,{"derivedFrom":[subQ1,subQ0]});Q80=makeQuery(id+"F0.imprint","IMPRINT",FACE,{"disambiguationData":[TD([[makeQuery(id+"F0.imprint","IMPRINT",EDGE,{"disambiguationData":[TD([[subQ2,-1.0]])],"derivedFrom":subQ1}),-1.0]])]});}
            var Q81;
            {var subQ0=sQuery(id+"F0.wireOp",EDGE,"E30.1.2");var subQ1=sQuery(id+"F0.wireOp",EDGE,"E12");var subQ2=makeQuery(id+"F0.imprint","INTERSECT",VERTEX,{"derivedFrom":[subQ1,subQ0]});Q81=makeQuery(id+"F0.imprint","IMPRINT",FACE,{"disambiguationData":[TD([[makeQuery(id+"F0.imprint","IMPRINT",EDGE,{"disambiguationData":[TD([[subQ2,-1.0]])],"derivedFrom":subQ1}),-1.0]])]});}
            var Q82;
            {var subQ0=sQuery(id+"F0.wireOp",EDGE,"E26");var subQ1=sQuery(id+"F0.wireOp",EDGE,"E12");var subQ2=makeQuery(id+"F0.imprint","INTERSECT",VERTEX,{"derivedFrom":[subQ1,subQ0]});Q82=makeQuery(id+"F0.imprint","IMPRINT",FACE,{"disambiguationData":[TD([[makeQuery(id+"F0.imprint","IMPRINT",EDGE,{"disambiguationData":[TD([[subQ2,-1.0]])],"derivedFrom":subQ1}),-1.0]])]});}
            var Q83;
            {var subQ0=sQuery(id+"F0.wireOp",EDGE,"E30.1.2");var subQ1=sQuery(id+"F0.wireOp",EDGE,"E13");var subQ2=makeQuery(id+"F0.imprint","INTERSECT",VERTEX,{"derivedFrom":[subQ1,subQ0]});Q83=makeQuery(id+"F0.imprint","IMPRINT",FACE,{"disambiguationData":[TD([[makeQuery(id+"F0.imprint","IMPRINT",EDGE,{"disambiguationData":[TD([[subQ2,-1.0]])],"derivedFrom":subQ1}),-1.0]])]});}
            var Q84;
            {var subQ0=sQuery(id+"F0.wireOp",EDGE,"E30.1.2");var subQ1=sQuery(id+"F0.wireOp",EDGE,"E14");var subQ2=makeQuery(id+"F0.imprint","INTERSECT",VERTEX,{"derivedFrom":[subQ1,subQ0]});Q84=makeQuery(id+"F0.imprint","IMPRINT",FACE,{"disambiguationData":[TD([[makeQuery(id+"F0.imprint","IMPRINT",EDGE,{"disambiguationData":[TD([[subQ2,-1.0]])],"derivedFrom":subQ1}),-1.0]])]});}
            var Q85;
            {var subQ0=sQuery(id+"F0.wireOp",EDGE,"E26");var subQ1=sQuery(id+"F0.wireOp",EDGE,"E14");var subQ2=makeQuery(id+"F0.imprint","INTERSECT",VERTEX,{"derivedFrom":[subQ1,subQ0]});Q85=makeQuery(id+"F0.imprint","IMPRINT",FACE,{"disambiguationData":[TD([[makeQuery(id+"F0.imprint","IMPRINT",EDGE,{"disambiguationData":[TD([[subQ2,-1.0]])],"derivedFrom":subQ1}),-1.0]])]});}
            var Q86;
            {var subQ0=sQuery(id+"F0.wireOp",EDGE,"E30.1.2");var subQ1=sQuery(id+"F0.wireOp",EDGE,"E15");var subQ2=makeQuery(id+"F0.imprint","INTERSECT",VERTEX,{"derivedFrom":[subQ1,subQ0]});Q86=makeQuery(id+"F0.imprint","IMPRINT",FACE,{"disambiguationData":[TD([[makeQuery(id+"F0.imprint","IMPRINT",EDGE,{"disambiguationData":[TD([[subQ2,-1.0]])],"derivedFrom":subQ1}),-1.0]])]});}
            var Q87;
            Q87=makeQuery(id+"F0.imprint","IMPRINT",FACE,{"disambiguationData":[TD([[makeQuery(id+"F0.imprint","IMPRINT",EDGE,{"derivedFrom":sQuery(id+"F0.wireOp",EDGE,"E19")}),-1.0]])]});
            var Q88;
            {var subQ0=sQuery(id+"F0.wireOp",EDGE,"E27");var subQ1=sQuery(id+"F0.wireOp",EDGE,"E15");var subQ2=makeQuery(id+"F0.imprint","INTERSECT",VERTEX,{"derivedFrom":[subQ1,subQ0]});Q88=makeQuery(id+"F0.imprint","IMPRINT",FACE,{"disambiguationData":[TD([[makeQuery(id+"F0.imprint","IMPRINT",EDGE,{"disambiguationData":[TD([[subQ2,-1.0]])],"derivedFrom":subQ1}),-1.0]])]});}
            var Q89;
            Q89=makeQuery(id+"F0.imprint","IMPRINT",FACE,{"disambiguationData":[TD([[makeQuery(id+"F0.imprint","IMPRINT",EDGE,{"derivedFrom":sQuery(id+"F0.wireOp",EDGE,"E20")}),-1.0]])]});
            var Q90;
            {var subQ0=sQuery(id+"F0.wireOp",EDGE,"E27");var subQ1=sQuery(id+"F0.wireOp",EDGE,"E13");var subQ2=makeQuery(id+"F0.imprint","INTERSECT",VERTEX,{"derivedFrom":[subQ1,subQ0]});Q90=makeQuery(id+"F0.imprint","IMPRINT",FACE,{"disambiguationData":[TD([[makeQuery(id+"F0.imprint","IMPRINT",EDGE,{"disambiguationData":[TD([[subQ2,-1.0]])],"derivedFrom":subQ1}),-1.0]])]});}
            var Q91;
            {var subQ0=sQuery(id+"F0.wireOp",EDGE,"E27");var subQ1=sQuery(id+"F0.wireOp",EDGE,"E12");var subQ2=makeQuery(id+"F0.imprint","INTERSECT",VERTEX,{"derivedFrom":[subQ1,subQ0]});Q91=makeQuery(id+"F0.imprint","IMPRINT",FACE,{"disambiguationData":[TD([[makeQuery(id+"F0.imprint","IMPRINT",EDGE,{"disambiguationData":[TD([[subQ2,-1.0]])],"derivedFrom":subQ1}),-1.0]])]});}
            var Q92;
            {var subQ0=sQuery(id+"F0.wireOp",EDGE,"E27");var subQ1=sQuery(id+"F0.wireOp",EDGE,"E14");var subQ2=makeQuery(id+"F0.imprint","INTERSECT",VERTEX,{"derivedFrom":[subQ1,subQ0]});Q92=makeQuery(id+"F0.imprint","IMPRINT",FACE,{"disambiguationData":[TD([[makeQuery(id+"F0.imprint","IMPRINT",EDGE,{"disambiguationData":[TD([[subQ2,-1.0]])],"derivedFrom":subQ1}),-1.0]])]});}
            var Q93;
            {var subQ0=sQuery(id+"F0.wireOp",EDGE,"E27");var subQ1=sQuery(id+"F0.wireOp",EDGE,"E11");var subQ2=makeQuery(id+"F0.imprint","INTERSECT",VERTEX,{"derivedFrom":[subQ1,subQ0]});Q93=makeQuery(id+"F0.imprint","IMPRINT",FACE,{"disambiguationData":[TD([[makeQuery(id+"F0.imprint","IMPRINT",EDGE,{"disambiguationData":[TD([[subQ2,-1.0]])],"derivedFrom":subQ1}),-1.0]])]});}
            var Q94;
            {var subQ0=sQuery(id+"F0.wireOp",EDGE,"E27");var subQ1=sQuery(id+"F0.wireOp",EDGE,"E10");var subQ2=makeQuery(id+"F0.imprint","INTERSECT",VERTEX,{"derivedFrom":[subQ1,subQ0]});Q94=makeQuery(id+"F0.imprint","IMPRINT",FACE,{"disambiguationData":[TD([[makeQuery(id+"F0.imprint","IMPRINT",EDGE,{"disambiguationData":[TD([[subQ2,-1.0]])],"derivedFrom":subQ1}),-1.0]])]});}
            var Q95;
            {var subQ0=sQuery(id+"F0.wireOp",EDGE,"E27");var subQ1=sQuery(id+"F0.wireOp",EDGE,"E9");var subQ2=makeQuery(id+"F0.imprint","INTERSECT",VERTEX,{"derivedFrom":[subQ1,subQ0]});Q95=makeQuery(id+"F0.imprint","IMPRINT",FACE,{"disambiguationData":[TD([[makeQuery(id+"F0.imprint","IMPRINT",EDGE,{"disambiguationData":[TD([[subQ2,-1.0]])],"derivedFrom":subQ1}),-1.0]])]});}
            var Q96;
            {var subQ0=sQuery(id+"F0.wireOp",EDGE,"E27");var subQ1=sQuery(id+"F0.wireOp",EDGE,"E8");var subQ2=makeQuery(id+"F0.imprint","INTERSECT",VERTEX,{"derivedFrom":[subQ1,subQ0]});Q96=makeQuery(id+"F0.imprint","IMPRINT",FACE,{"disambiguationData":[TD([[makeQuery(id+"F0.imprint","IMPRINT",EDGE,{"disambiguationData":[TD([[subQ2,-1.0]])],"derivedFrom":subQ1}),-1.0]])]});}
            var Q97;
            {var subQ0=sQuery(id+"F0.wireOp",EDGE,"E27");var subQ1=sQuery(id+"F0.wireOp",EDGE,"E7");var subQ2=makeQuery(id+"F0.imprint","INTERSECT",VERTEX,{"derivedFrom":[subQ1,subQ0]});Q97=makeQuery(id+"F0.imprint","IMPRINT",FACE,{"disambiguationData":[TD([[makeQuery(id+"F0.imprint","IMPRINT",EDGE,{"disambiguationData":[TD([[subQ2,-1.0]])],"derivedFrom":subQ1}),-1.0]])]});}
            var Q98;
            {var subQ0=sQuery(id+"F0.wireOp",EDGE,"E27");var subQ1=sQuery(id+"F0.wireOp",EDGE,"E6");var subQ2=makeQuery(id+"F0.imprint","INTERSECT",VERTEX,{"derivedFrom":[subQ1,subQ0]});Q98=makeQuery(id+"F0.imprint","IMPRINT",FACE,{"disambiguationData":[TD([[makeQuery(id+"F0.imprint","IMPRINT",EDGE,{"disambiguationData":[TD([[subQ2,-1.0]])],"derivedFrom":subQ1}),-1.0]])]});}
            var Q99;
            {var subQ0=sQuery(id+"F0.wireOp",EDGE,"E27");var subQ1=sQuery(id+"F0.wireOp",EDGE,"E5");var subQ2=makeQuery(id+"F0.imprint","INTERSECT",VERTEX,{"derivedFrom":[subQ1,subQ0]});Q99=makeQuery(id+"F0.imprint","IMPRINT",FACE,{"disambiguationData":[TD([[makeQuery(id+"F0.imprint","IMPRINT",EDGE,{"disambiguationData":[TD([[subQ2,-1.0]])],"derivedFrom":subQ1}),-1.0]])]});}
            var Q100;
            {var subQ0=sQuery(id+"F0.wireOp",EDGE,"E27");var subQ1=sQuery(id+"F0.wireOp",EDGE,"E4");var subQ2=makeQuery(id+"F0.imprint","INTERSECT",VERTEX,{"derivedFrom":[subQ1,subQ0]});Q100=makeQuery(id+"F0.imprint","IMPRINT",FACE,{"disambiguationData":[TD([[makeQuery(id+"F0.imprint","IMPRINT",EDGE,{"disambiguationData":[TD([[subQ2,-1.0]])],"derivedFrom":subQ1}),-1.0]])]});}
            var Q101;
            {var subQ0=sQuery(id+"F0.wireOp",EDGE,"E27");var subQ1=sQuery(id+"F0.wireOp",EDGE,"E3");var subQ2=makeQuery(id+"F0.imprint","INTERSECT",VERTEX,{"derivedFrom":[subQ1,subQ0]});Q101=makeQuery(id+"F0.imprint","IMPRINT",FACE,{"disambiguationData":[TD([[makeQuery(id+"F0.imprint","IMPRINT",EDGE,{"disambiguationData":[TD([[subQ2,-1.0]])],"derivedFrom":subQ1}),-1.0]])]});}
            var Q102;
            {var subQ0=sQuery(id+"F0.wireOp",EDGE,"E27");var subQ1=sQuery(id+"F0.wireOp",EDGE,"E2");var subQ2=makeQuery(id+"F0.imprint","INTERSECT",VERTEX,{"derivedFrom":[subQ1,subQ0]});Q102=makeQuery(id+"F0.imprint","IMPRINT",FACE,{"disambiguationData":[TD([[makeQuery(id+"F0.imprint","IMPRINT",EDGE,{"disambiguationData":[TD([[subQ2,-1.0]])],"derivedFrom":subQ1}),-1.0]])]});}
            var Q103;
            {var subQ0=sQuery(id+"F0.wireOp",EDGE,"E27");var subQ1=sQuery(id+"F0.wireOp",EDGE,"E1");var subQ2=makeQuery(id+"F0.imprint","INTERSECT",VERTEX,{"derivedFrom":[subQ1,subQ0]});Q103=makeQuery(id+"F0.imprint","IMPRINT",FACE,{"disambiguationData":[TD([[makeQuery(id+"F0.imprint","IMPRINT",EDGE,{"disambiguationData":[TD([[subQ2,-1.0]])],"derivedFrom":subQ1}),-1.0]])]});}
            var Q104;
            {var subQ0=sQuery(id+"F0.wireOp",EDGE,"E27");var subQ1=sQuery(id+"F0.wireOp",EDGE,"E0");var subQ2=makeQuery(id+"F0.imprint","INTERSECT",VERTEX,{"derivedFrom":[subQ1,subQ0]});Q104=makeQuery(id+"F0.imprint","IMPRINT",FACE,{"disambiguationData":[TD([[makeQuery(id+"F0.imprint","IMPRINT",EDGE,{"disambiguationData":[TD([[subQ2,-1.0]])],"derivedFrom":subQ1}),-1.0]])]});}
            extrude(context, id + "F1", {"entities" : qUnion([Q0, Q1, Q2, Q3, Q4, Q5, Q6, Q7, Q8, Q9, Q10, Q11, Q12, Q13, Q14, Q15, Q16, Q17, Q18, Q19, Q20, Q21, Q22, Q23, Q24, Q25, Q26, Q27, Q28, Q29, Q30, Q31, Q32, Q33, Q34, Q35, Q36, Q37, Q38, Q39, Q40, Q41, Q42, Q43, Q44, Q45, Q46, Q47, Q48, Q49, Q50, Q51, Q52, Q53, Q54, Q55, Q56, Q57, Q58, Q59, Q60, Q61, Q62, Q63, Q64, Q65, Q66, Q67, Q68, Q69, Q70, Q71, Q72, Q73, Q74, Q75, Q76, Q77, Q78, Q79, Q80, Q81, Q82, Q83, Q84, Q85, Q86, Q87, Q88, Q89, Q90, Q91, Q92, Q93, Q94, Q95, Q96, Q97, Q98, Q99, Q100, Q101, Q102, Q103, Q104]), "depth" : 1 * mm, "offsetDistance" : 25 * mm});
        }
        {
            var Q0;
            Q0=makeQuery(id+"F1.opExtrude","CAP_FACE",FACE,{"disambiguationData":[OSD([sQuery(id+"F0.wireOp",EDGE,"E0"),sQuery(id+"F0.wireOp",EDGE,"E1"),sQuery(id+"F0.wireOp",EDGE,"E2"),sQuery(id+"F0.wireOp",EDGE,"E3"),sQuery(id+"F0.wireOp",EDGE,"E4"),sQuery(id+"F0.wireOp",EDGE,"E5"),sQuery(id+"F0.wireOp",EDGE,"E6"),sQuery(id+"F0.wireOp",EDGE,"E7"),sQuery(id+"F0.wireOp",EDGE,"E8"),sQuery(id+"F0.wireOp",EDGE,"E9"),sQuery(id+"F0.wireOp",EDGE,"E10"),sQuery(id+"F0.wireOp",EDGE,"E11"),sQuery(id+"F0.wireOp",EDGE,"E12"),sQuery(id+"F0.wireOp",EDGE,"E13"),sQuery(id+"F0.wireOp",EDGE,"E14"),sQuery(id+"F0.wireOp",EDGE,"E15"),sQuery(id+"F0.wireOp",EDGE,"E17"),sQuery(id+"F0.wireOp",EDGE,"E18"),sQuery(id+"F0.wireOp",EDGE,"E19"),sQuery(id+"F0.wireOp",EDGE,"E20"),sQuery(id+"F0.wireOp",EDGE,"E21"),sQuery(id+"F0.wireOp",EDGE,"E22"),sQuery(id+"F0.wireOp",EDGE,"E23"),sQuery(id+"F0.wireOp",EDGE,"E24"),sQuery(id+"F0.wireOp",EDGE,"E26"),sQuery(id+"F0.wireOp",EDGE,"E27"),sQuery(id+"F0.wireOp",EDGE,"E28"),sQuery(id+"F0.wireOp",EDGE,"E29"),sQuery(id+"F0.wireOp",EDGE,"E30.1.0"),sQuery(id+"F0.wireOp",EDGE,"E30.1.2"),sQuery(id+"F0.wireOp",EDGE,"E30.1.3"),sQuery(id+"F0.wireOp",EDGE,"E30.1.4")])],"isStart":true});
            var Q1;
            Q1=makeQuery(id+"F1.opExtrude","CAP_FACE",FACE,{"disambiguationData":[OSD([sQuery(id+"F0.wireOp",EDGE,"E0"),sQuery(id+"F0.wireOp",EDGE,"E1"),sQuery(id+"F0.wireOp",EDGE,"E2"),sQuery(id+"F0.wireOp",EDGE,"E3"),sQuery(id+"F0.wireOp",EDGE,"E4"),sQuery(id+"F0.wireOp",EDGE,"E5"),sQuery(id+"F0.wireOp",EDGE,"E6"),sQuery(id+"F0.wireOp",EDGE,"E7"),sQuery(id+"F0.wireOp",EDGE,"E8"),sQuery(id+"F0.wireOp",EDGE,"E9"),sQuery(id+"F0.wireOp",EDGE,"E10"),sQuery(id+"F0.wireOp",EDGE,"E11"),sQuery(id+"F0.wireOp",EDGE,"E12"),sQuery(id+"F0.wireOp",EDGE,"E13"),sQuery(id+"F0.wireOp",EDGE,"E14"),sQuery(id+"F0.wireOp",EDGE,"E15"),sQuery(id+"F0.wireOp",EDGE,"E17"),sQuery(id+"F0.wireOp",EDGE,"E18"),sQuery(id+"F0.wireOp",EDGE,"E19"),sQuery(id+"F0.wireOp",EDGE,"E20"),sQuery(id+"F0.wireOp",EDGE,"E21"),sQuery(id+"F0.wireOp",EDGE,"E22"),sQuery(id+"F0.wireOp",EDGE,"E23"),sQuery(id+"F0.wireOp",EDGE,"E24"),sQuery(id+"F0.wireOp",EDGE,"E26"),sQuery(id+"F0.wireOp",EDGE,"E27"),sQuery(id+"F0.wireOp",EDGE,"E28"),sQuery(id+"F0.wireOp",EDGE,"E29"),sQuery(id+"F0.wireOp",EDGE,"E30.1.0"),sQuery(id+"F0.wireOp",EDGE,"E30.1.2"),sQuery(id+"F0.wireOp",EDGE,"E30.1.3"),sQuery(id+"F0.wireOp",EDGE,"E30.1.4")])],"isStart":false});
            fillet(context, id + "F2", {"entities" : qUnion([Q0, Q1]), "radius" : 0.5 * mm, "tangentPropagation" : true, "allowEdgeOverflow" : false});
        }
    });
